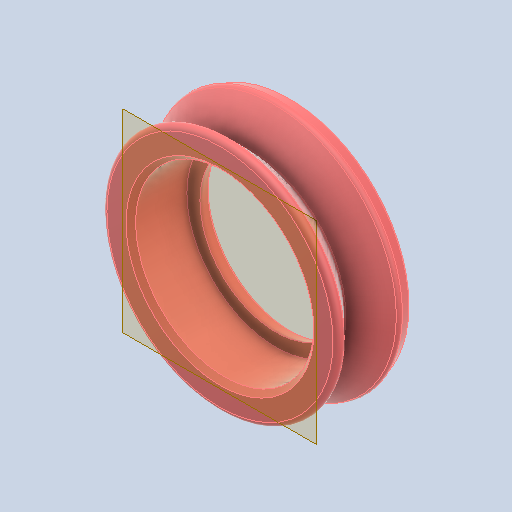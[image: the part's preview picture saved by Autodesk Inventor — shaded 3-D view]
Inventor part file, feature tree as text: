
AUTODESK INVENTOR PART (.ipt)
format: ipt  version: 2022 (Build 260153000, 153)  size: 434,176 bytes
history: native  units: in
note: dims shown in document units (in); Inventor stores cm internally (conversion verified against a paired STEP export)
features: other x2, plane x1, revolve x1, fillet x1, chamfer x1, sketch x1
ambient origin geometry x8: Origin, YZ Plane, XZ Plane, XY Plane, X Axis, Y Axis, Z Axis, Center Point
bodies: Solid1 (feature_tree)
feature tree (7):
  plane  "Work Plane1"
  revolve  "Revolution1"  [1 undecoded]
  fillet  "Fillet1"  [1 undecoded]
  chamfer  "Chamfer1"  Angle=45.0deg  [1 undecoded]
  sketch  "Sketch1"  dims[d0=0.876in d1=0.2756in d3=45.0deg d4=45.0deg d6=0.481in d7=0.0787in d8=0.748in d9=0.481in d10=90.0deg d11=0.0236in d12=0.0236in d13=0.125in d14=45.0deg d16=0.0394in d17=1.2244in]
  other  "<userpath>\Documents\CAD\guardSwerve1\Assembly1.iam"
  other  "Assembly1.iam"
note: 3 required parameter values undecoded (feature->parameter linkage not recoverable at this tier; creation-order binding heuristic only, values carry confidence <= 0.55)